FCSTD DOCUMENT  (FreeCAD 0.20R0.20.2)
Label: 0.004
License: All rights reserved
LicenseURL: http://en.wikipedia.org/wiki/All_rights_reserved
objects: Sketcher::SketchObject×1
note: 1 computed .brp shape members not serialized (recipe doc carries the construction recipe); baked Part::Feature solids carry a one-line shape summary decoded from their .brp

FEATURE [Sketcher::SketchObject] Sketch
  FullyConstrained = true
  sketch-geometry (25):
    g0: Circle CenterX=0 CenterY=0 CenterZ=0 NormalX=0 NormalY=0 NormalZ=1 AngleXU=0 Radius=0.9
    g1: LineSegment StartX=0 StartY=0 StartZ=0 EndX=12 EndY=0 EndZ=0
    g2: LineSegment StartX=0 StartY=0 StartZ=0 EndX=-12 EndY=0 EndZ=0
    g3: LineSegment StartX=12 StartY=0 StartZ=0 EndX=12 EndY=38 EndZ=0
    g4: LineSegment StartX=12 StartY=0 StartZ=0 EndX=12 EndY=-38 EndZ=0
    g5: LineSegment StartX=12 StartY=38 StartZ=0 EndX=9 EndY=38 EndZ=0
    g6: LineSegment StartX=12 StartY=-38 StartZ=0 EndX=9 EndY=-38 EndZ=0
    g7: LineSegment StartX=-12 StartY=0 StartZ=0 EndX=-12 EndY=6 EndZ=0
    g8: LineSegment StartX=-12 StartY=0 StartZ=0 EndX=-12 EndY=-6 EndZ=0
    g9: Circle CenterX=-12 CenterY=6 CenterZ=0 NormalX=0 NormalY=0 NormalZ=1 AngleXU=0 Radius=1
    g10: Circle CenterX=6 CenterY=16 CenterZ=0 NormalX=0 NormalY=0 NormalZ=1 AngleXU=0 Radius=1
    g11: Circle CenterX=9 CenterY=38 CenterZ=0 NormalX=0 NormalY=0 NormalZ=1 AngleXU=0 Radius=1
    g12: BSplineCurve PolesCount=3 KnotsCount=2 Degree=2 IsPeriodic=0
    g13: GeomPoint X=-12 Y=6 Z=0
    g14: GeomPoint X=9 Y=38 Z=0
    g15: Circle CenterX=-12 CenterY=-6 CenterZ=0 NormalX=0 NormalY=0 NormalZ=1 AngleXU=0 Radius=1
    g16: Circle CenterX=6 CenterY=-16 CenterZ=0 NormalX=0 NormalY=0 NormalZ=1 AngleXU=0 Radius=1
    g17: Circle CenterX=9 CenterY=-38 CenterZ=0 NormalX=0 NormalY=0 NormalZ=1 AngleXU=0 Radius=1
    g18: BSplineCurve PolesCount=3 KnotsCount=2 Degree=2 IsPeriodic=0
    g19: GeomPoint X=-12 Y=-6 Z=0
    g20: GeomPoint X=9 Y=-38 Z=0
    g21: Circle CenterX=6 CenterY=12 CenterZ=0 NormalX=0 NormalY=0 NormalZ=1 AngleXU=0 Radius=4
    g22: Circle CenterX=6 CenterY=-12 CenterZ=0 NormalX=0 NormalY=0 NormalZ=1 AngleXU=0 Radius=4
    g23: Circle CenterX=9 CenterY=-24 CenterZ=0 NormalX=0 NormalY=0 NormalZ=1 AngleXU=0 Radius=2
    g24: Circle CenterX=9 CenterY=24 CenterZ=0 NormalX=0 NormalY=0 NormalZ=1 AngleXU=0 Radius=2
  constraints (53):
    c: Block(g0)
    c: Coincident(g1,g0)
    c: Horizontal(g1)
    c: Distance(g1) = 12
    c: Coincident(g2,g0)
    c: Horizontal(g2)
    c: Distance(g2) = 12
    c: Coincident(g3,g1)
    c: Vertical(g3)
    c: Distance(g3) = 38
    c: Coincident(g4,g1)
    c: Vertical(g4)
    c: Distance(g4) = 38
    c: Coincident(g5,g3)
    c: Horizontal(g5)
    c: Coincident(g6,g4)
    c: Horizontal(g6)
    c: Distance(g6) = 3
    c: Distance(g5) = 3
    c: Coincident(g7,g2)
    c: Vertical(g7)
    c: Coincident(g8,g2)
    c: Vertical(g8)
    c: Distance(g7) = 6
    c: Distance(g8) = 6
    c: Weight(g9) = 1
    c: Coincident(g12,g7)
    c: Equal(g9,g10)
    c: Equal(g9,g11)
    c: Coincident(g12,g5)
    c: InternalAlignment(g9,g12)
    c: InternalAlignment(g10,g12)
    c: InternalAlignment(g11,g12)
    c: InternalAlignment(g13,g12)
    c: InternalAlignment(g14,g12)
    c: Weight(g15) = 1
    c: Coincident(g18,g8)
    c: Equal(g15,g16)
    c: Equal(g15,g17)
    c: Coincident(g18,g6)
    c: InternalAlignment(g15,g18)
    c: InternalAlignment(g16,g18)
    c: InternalAlignment(g17,g18)
    c: InternalAlignment(g19,g18)
    c: InternalAlignment(g20,g18)
    c: PointOnObject(g10,g21)
    c: PointOnObject(g16,g22)
    c: Block(g21)
    c: Block(g24)
    c: Block(g12)
    c: Block(g18)
    c: Block(g22)
    c: Block(g23)
